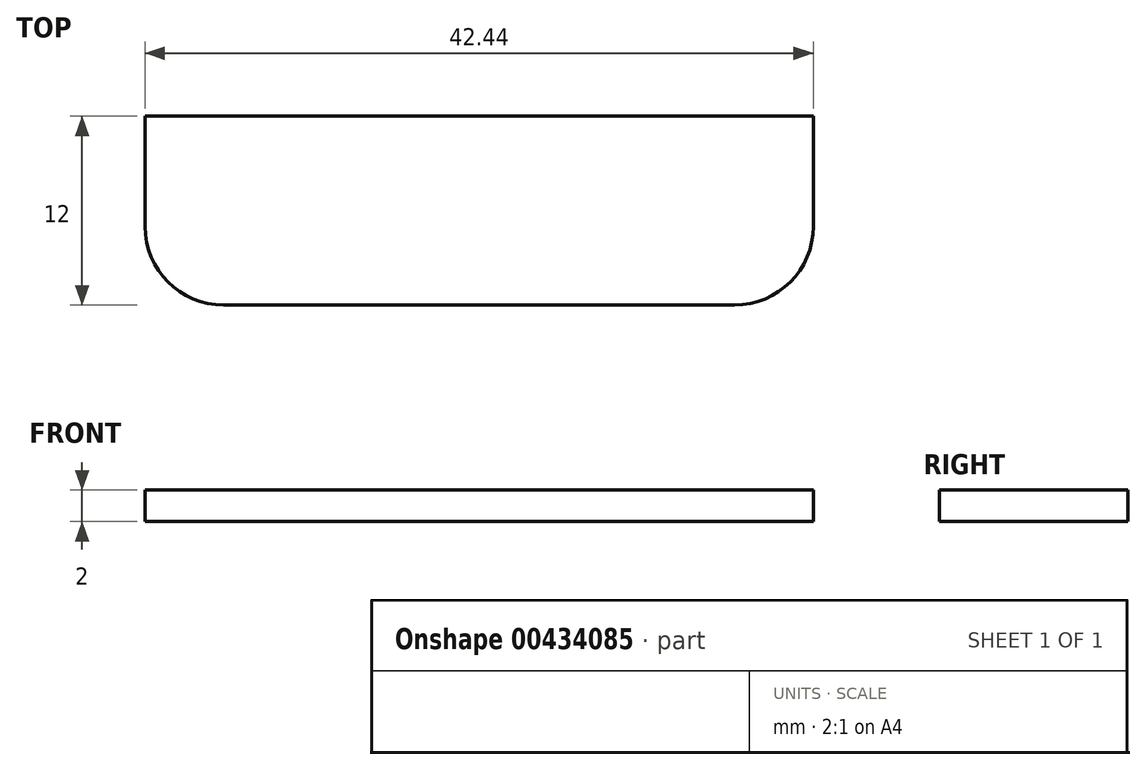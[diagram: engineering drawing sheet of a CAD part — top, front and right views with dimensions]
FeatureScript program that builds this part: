
annotation { "Feature Type Name" : "Feature", "Feature Type Description" : "" }
export const myFeature = defineFeature(function(context is Context, id is Id, definition is map)
    precondition{}
    {
        {
            var Q0;
            Q0=qCreatedBy(makeId("Top.planeOp"),FACE);
            var sketch = newSketch(context, id + "F0", { "sketchPlane" : qUnion([Q0])});
            skLineSegment(sketch, "E0.bottom", {"start": v(-22.78, 7.44) * mm, "end": v(19.66, 7.44) * mm});
            skLineSegment(sketch, "E0.top", {"start": v(-17.78, -4.56) * mm, "end": v(14.66, -4.56) * mm});
            skLineSegment(sketch, "E0.left", {"start": v(-22.78, 7.44) * mm, "end": v(-22.78, 0.44) * mm});
            skLineSegment(sketch, "E0.right", {"start": v(19.66, 7.44) * mm, "end": v(19.66, 0.44) * mm});
            skPoint(sketch, "E1.visualSharp", {"position": v(-22.78, -4.56) * mm});
            skArc(sketch, "E1.filletArc", {"start": v(-22.78, 0.44) * mm, "mid": v(-21.32, -3.1) * mm, "end": v(-17.78, -4.56) * mm});
            skPoint(sketch, "E2.visualSharp", {"position": v(19.66, -4.56) * mm});
            skArc(sketch, "E2.filletArc", {"start": v(14.66, -4.56) * mm, "mid": v(18.2, -3.1) * mm, "end": v(19.66, 0.44) * mm});
            skSolve(sketch);
        }
        {
            var Q0;
            Q0=makeQuery(id+"F0.imprint","IMPRINT",FACE,{"disambiguationData":[TD([[makeQuery(id+"F0.imprint","IMPRINT",EDGE,{"derivedFrom":sQuery(id+"F0.wireOp",EDGE,"E0.bottom")}),-1.0]])]});
            extrude(context, id + "F1", {"entities" : qUnion([Q0]), "depth" : 2 * mm, "offsetDistance" : 25 * mm});
        }
    });
